FCSTD DOCUMENT  (FreeCAD 1.0R39109 (Git))
Label: capinet hook
License: All rights reserved
LicenseURL: https://en.wikipedia.org/wiki/All_rights_reserved
objects: Sketcher::SketchObject×1, PartDesign::Body×1
note: 3 computed .brp shape members not serialized (recipe doc carries the construction recipe); baked Part::Feature solids carry a one-line shape summary decoded from their .brp

FEATURE [Sketcher::SketchObject] Sketch
  ArcFitTolerance = 1e-06
  AttachmentSupport = -> [XY_Plane]
  FullyConstrained = false
  MakeInternals = false
  MapMode = 5
  sketch-geometry (11):
    g0: ArcOfCircle CenterX=0 CenterY=0 CenterZ=0 NormalX=0 NormalY=0 NormalZ=1 AngleXU=0 Radius=13 StartAngle=5.88839 EndAngle=9.81957
    g1: ArcOfCircle CenterX=0 CenterY=0 CenterZ=0 NormalX=0 NormalY=0 NormalZ=1 AngleXU=0 Radius=18 StartAngle=5.88839 EndAngle=9.92678
    g2: ArcOfCircle CenterX=14.3077 CenterY=-5.96154 CenterZ=0 NormalX=0 NormalY=0 NormalZ=1 AngleXU=0 Radius=2.5 StartAngle=2.7468 EndAngle=5.88839
    g3: LineSegment StartX=-25.6124 StartY=-33.8986 StartZ=0 EndX=-2.50105 EndY=-49.4753 EndZ=0
    g4: LineSegment StartX=-2.50105 StartY=-49.4753 StartZ=0 EndX=8.25034 EndY=-30.8385 EndZ=0
    g5: LineSegment StartX=8.25034 StartY=-30.8385 StartZ=0 EndX=-12 EndY=-5 EndZ=0
    g6: LineSegment StartX=-15.7792 StartY=-8.66131 StartZ=0 EndX=-10.5993 EndY=-18.098 EndZ=0
    g7: LineSegment StartX=-10.5993 StartY=-18.098 StartZ=0 EndX=2.08897 EndY=-31.204 EndZ=0
    g8: LineSegment StartX=2.08897 StartY=-31.204 StartZ=0 EndX=-3.23695 EndY=-37.1565 EndZ=0
    g9: LineSegment StartX=-3.23695 StartY=-37.1565 StartZ=0 EndX=-19.6509 EndY=-25.3413 EndZ=0
    g10: ArcOfCircle CenterX=-22.6977 CenterY=-29.574 CenterZ=0 NormalX=0 NormalY=0 NormalZ=1 AngleXU=0 Radius=5.21515 StartAngle=0.94689 EndAngle=4.11934
  constraints (17):
    c: Coincident(g0,g-1)
    c: Diameter(g0) = 26
    c: Horizontal(g0,g0)
    c: DistanceX(g0,g0) = 24
    c: Tangent(g2,g1) = -1.5708
    c: Tangent(g2,g0) = 1.5708
    c: Diameter(g2) = 5
    c: Coincident(g3,g4)
    c: Coincident(g4,g5)
    c: Coincident(g5,g0)
    c: Tangent(g1,g6) = -1.5708
    c: Coincident(g6,g7)
    c: Coincident(g7,g8)
    c: Coincident(g8,g9)
    c: Coincident(g1,g0)
    c: Tangent(g9,g10) = -1.5708
    c: Tangent(g10,g3) = -1.5708
FEATURE [PartDesign::Body] Body
  AllowCompound = false
  Group = -> [Sketch]
  Origin = -> Origin
